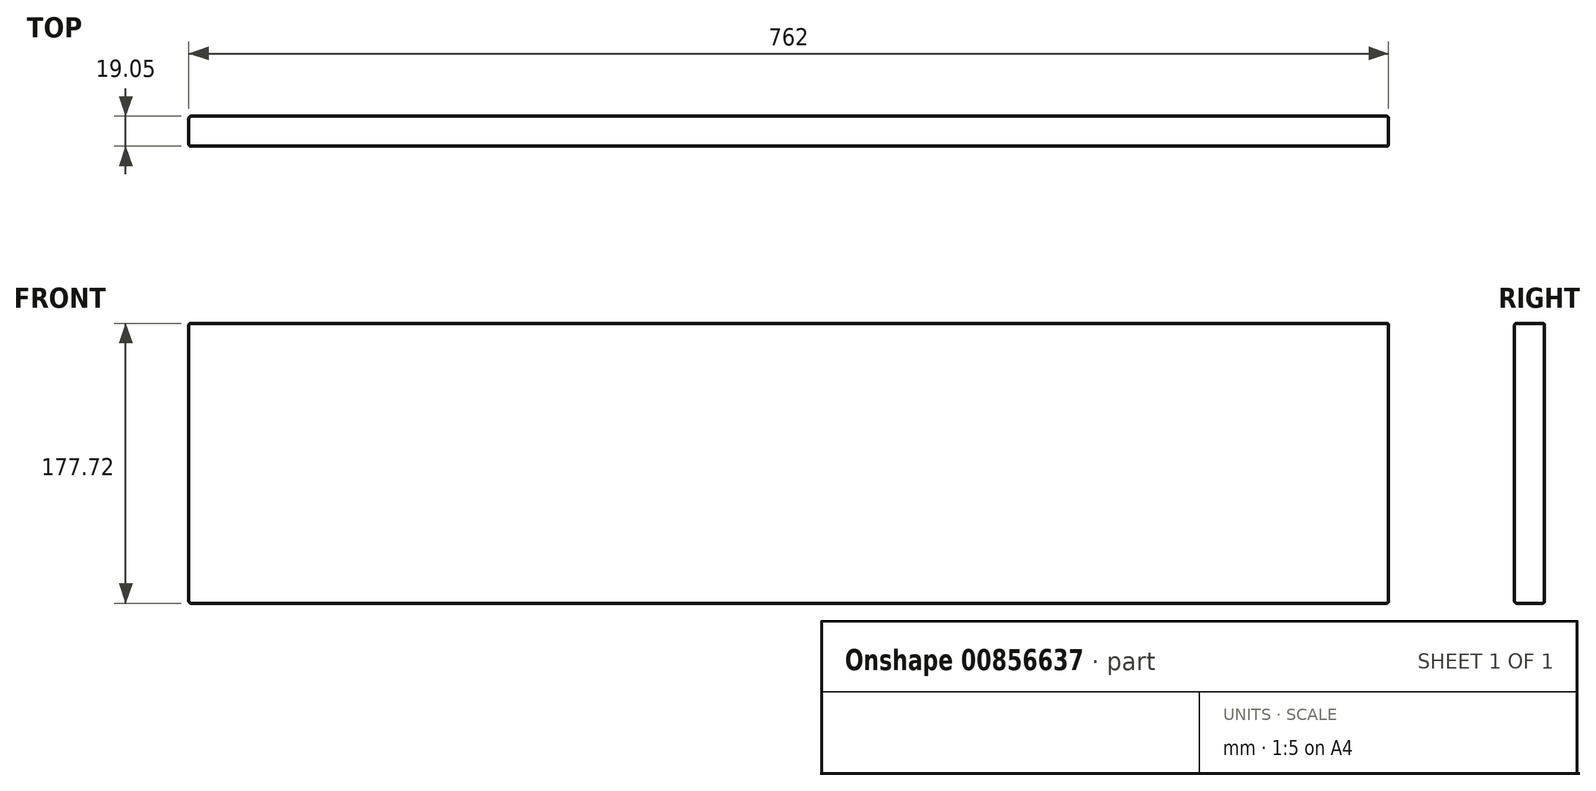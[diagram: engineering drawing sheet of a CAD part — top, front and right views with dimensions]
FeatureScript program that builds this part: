
annotation { "Feature Type Name" : "Feature", "Feature Type Description" : "" }
export const myFeature = defineFeature(function(context is Context, id is Id, definition is map)
    precondition{}
    {
        {
            var Q0;
            Q0=qCreatedBy(makeId("Front.planeOp"),FACE);
            var sketch = newSketch(context, id + "F0", { "sketchPlane" : qUnion([Q0])});
            skLineSegment(sketch, "E0.bottom", {"start": v(1208.67, 0) * mm, "end": v(2113.54, 0) * mm});
            skLineSegment(sketch, "E0.top", {"start": v(1208.67, 1778) * mm, "end": v(2113.54, 1778) * mm});
            skLineSegment(sketch, "E0.left", {"start": v(1208.67, 0) * mm, "end": v(1208.67, 1778) * mm});
            skLineSegment(sketch, "E0.right", {"start": v(2113.54, 0) * mm, "end": v(2113.54, 1778) * mm});
            skLineSegment(sketch, "E1.left", {"start": v(0, 0) * mm, "end": v(0.1, 863.6) * mm});
            skLineSegment(sketch, "E1.right", {"start": v(-1905, -2.15) * mm, "end": v(-1904.9, 861.45) * mm});
            skLineSegment(sketch, "E2.top", {"start": v(0.1, 901.7) * mm, "end": v(-2504.34, 901.7) * mm});
            skLineSegment(sketch, "E2.left", {"start": v(0.1, 863.6) * mm, "end": v(0.1, 901.7) * mm});
            skLineSegment(sketch, "E2.right", {"start": v(-2504.34, 863.6) * mm, "end": v(-2504.34, 901.7) * mm});
            skLineSegment(sketch, "E3", {"start": v(-1904.9, 1058.57) * mm, "end": v(-1904.9, -228.77) * mm, "construction": true});
            skLineSegment(sketch, "E4", {"start": v(0, 1058.57) * mm, "end": v(0, -228.77) * mm, "construction": true});
            skLineSegment(sketch, "E5.bottom", {"start": v(0, 0) * mm, "end": v(-381, 0) * mm});
            skLineSegment(sketch, "E5.left", {"start": v(0, 0) * mm, "end": v(0, 857.25) * mm});
            skLineSegment(sketch, "E6", {"start": v(-381, 0) * mm, "end": v(-387.35, 0) * mm, "construction": true});
            skLineSegment(sketch, "E7.bottom", {"start": v(-387.35, 0) * mm, "end": v(-1143, 0) * mm, "construction": true});
            skLineSegment(sketch, "E7.left", {"start": v(-387.35, 0) * mm, "end": v(-387.35, 736.6) * mm, "construction": true});
            skLineSegment(sketch, "E8", {"start": v(0, 0) * mm, "end": v(-1905, -2.15) * mm, "construction": true});
            skLineSegment(sketch, "E9.bottom", {"start": v(-387.35, 857.25) * mm, "end": v(-1143, 857.25) * mm, "construction": true});
            skLineSegment(sketch, "E9.top", {"start": v(-387.35, 121.5) * mm, "end": v(-1143, 120.65) * mm, "construction": true});
            skLineSegment(sketch, "E9.left", {"start": v(-387.35, 857.25) * mm, "end": v(-387.35, 121.5) * mm, "construction": true});
            skLineSegment(sketch, "E9.right", {"start": v(-1143, 857.25) * mm, "end": v(-1143, 120.65) * mm, "construction": true});
            skLineSegment(sketch, "E10", {"start": v(-1149.35, 857.25) * mm, "end": v(-1149.35, 120.65) * mm, "construction": true});
            skLineSegment(sketch, "E11.bottom", {"start": v(-1149.35, 857.25) * mm, "end": v(-1527.18, 857.25) * mm});
            skLineSegment(sketch, "E11.top", {"start": v(-1149.35, 82.55) * mm, "end": v(-1527.18, 82.55) * mm});
            skLineSegment(sketch, "E11.left", {"start": v(-1149.35, 857.25) * mm, "end": v(-1149.35, 82.55) * mm});
            skLineSegment(sketch, "E11.right", {"start": v(-1527.18, 857.25) * mm, "end": v(-1527.18, 82.55) * mm});
            skLineSegment(sketch, "E12", {"start": v(-1527.18, 82.55) * mm, "end": v(-1533.53, 82.54) * mm, "construction": true});
            skLineSegment(sketch, "E13.bottom", {"start": v(-1533.53, 82.54) * mm, "end": v(-1911.35, 82.54) * mm});
            skLineSegment(sketch, "E13.top", {"start": v(-1533.53, 857.25) * mm, "end": v(-1911.35, 857.25) * mm});
            skLineSegment(sketch, "E13.left", {"start": v(-1533.53, 82.54) * mm, "end": v(-1533.53, 857.25) * mm});
            skLineSegment(sketch, "E13.right", {"start": v(-1911.35, 82.54) * mm, "end": v(-1911.35, 857.25) * mm});
            skLineSegment(sketch, "E14", {"start": v(0, 857.25) * mm, "end": v(-2682.58, 857.25) * mm, "construction": true});
            skLineSegment(sketch, "E15.bottom", {"start": v(0, 857.25) * mm, "end": v(-381, 857.25) * mm});
            skLineSegment(sketch, "E15.top", {"start": v(0, 82.55) * mm, "end": v(-381, 82.55) * mm});
            skLineSegment(sketch, "E15.left", {"start": v(0, 857.25) * mm, "end": v(0, 82.55) * mm});
            skLineSegment(sketch, "E15.right", {"start": v(-381, 857.25) * mm, "end": v(-381, 82.55) * mm});
            skLineSegment(sketch, "E16.bottom", {"start": v(-387.35, 82.55) * mm, "end": v(-1143, 82.55) * mm});
            skLineSegment(sketch, "E16.top", {"start": v(-387.35, 115.22) * mm, "end": v(-1143, 115.22) * mm});
            skLineSegment(sketch, "E16.left", {"start": v(-387.35, 82.55) * mm, "end": v(-387.35, 115.22) * mm});
            skLineSegment(sketch, "E16.right", {"start": v(-1143, 82.55) * mm, "end": v(-1143, 115.22) * mm});
            skPoint(sketch, "E17", {"position": v(-765.18, 121.08) * mm});
            skPoint(sketch, "E18", {"position": v(-1530.35, 82.55) * mm});
            skPoint(sketch, "E18.positionSnap0", {"position": v(-1530.35, 82.55) * mm});
            skLineSegment(sketch, "E19", {"start": v(-765.18, 121.08) * mm, "end": v(-765.18, 1778) * mm, "construction": true});
            skLineSegment(sketch, "E20.bottom", {"start": v(-384.18, 2133.52) * mm, "end": v(-1146.18, 2133.52) * mm, "construction": true});
            skPoint(sketch, "E20.middle", {"position": v(-765.18, 1778) * mm});
            skLineSegment(sketch, "E21.bottom", {"start": v(-2504.34, 2438.4) * mm, "end": v(-1146.18, 2438.4) * mm});
            skLineSegment(sketch, "E21.top", {"start": v(-2504.34, 1778) * mm, "end": v(-1146.18, 1778) * mm});
            skLineSegment(sketch, "E21.left", {"start": v(-2504.34, 2438.4) * mm, "end": v(-2504.34, 1778) * mm});
            skLineSegment(sketch, "E21.right", {"start": v(-1146.18, 2438.4) * mm, "end": v(-1146.18, 1778) * mm});
            skLineSegment(sketch, "E22.bottom", {"start": v(0, 2438.4) * mm, "end": v(-384.18, 2438.4) * mm});
            skLineSegment(sketch, "E22.top", {"start": v(0, 1778) * mm, "end": v(-384.18, 1778) * mm});
            skLineSegment(sketch, "E22.left", {"start": v(0, 2438.4) * mm, "end": v(0, 1778) * mm});
            skLineSegment(sketch, "E22.right", {"start": v(-384.18, 2438.4) * mm, "end": v(-384.18, 1778) * mm});
            skLineSegment(sketch, "E23.bottom", {"start": v(-1146.18, 2133.52) * mm, "end": v(-384.18, 2133.52) * mm});
            skLineSegment(sketch, "E23.top", {"start": v(-1146.18, 1955.8) * mm, "end": v(-384.18, 1955.8) * mm});
            skLineSegment(sketch, "E23.left", {"start": v(-1146.18, 2133.52) * mm, "end": v(-1146.18, 1955.8) * mm});
            skLineSegment(sketch, "E23.right", {"start": v(-384.18, 2133.52) * mm, "end": v(-384.18, 1955.8) * mm});
            skLineSegment(sketch, "E24.bottom", {"start": v(-384.18, 1778) * mm, "end": v(0, 1778) * mm});
            skSolve(sketch);
        }
        {
            var Q0;
            {var subQ2=sQuery(id+"F0.wireOp",EDGE,"E23.bottom");Q0=makeQuery(id+"F0.imprint","IMPRINT",FACE,{"disambiguationData":[TD([[makeQuery(id+"F0.imprint","IMPRINT",EDGE,{"derivedFrom":subQ2}),-1.0]])]});}
            extrude(context, id + "F1", {"entities" : qUnion([Q0]), "depth" : 19.05 * mm, "offsetDistance" : 25.4 * mm});
        }
        {
            var Q0;
            Q0=makeQuery(id+"F1.opExtrude","CAP_FACE",FACE,{"disambiguationData":[OSD([sQuery(id+"F0.wireOp",EDGE,"E21.right"),sQuery(id+"F0.wireOp",EDGE,"E22.right"),sQuery(id+"F0.wireOp",EDGE,"E23.bottom"),sQuery(id+"F0.wireOp",EDGE,"E23.top")])],"isStart":false});
            var Q1;
            Q1=makeQuery(id+"F1.opExtrude","SWEPT_FACE",FACE,{"disambiguationData":[OSD([sQuery(id+"F0.wireOp",EDGE,"E23.bottom")])]});
            var Q2;
            Q2=makeQuery(id+"F1.opExtrude","SWEPT_FACE",FACE,{"disambiguationData":[OSD([sQuery(id+"F0.wireOp",EDGE,"E21.right")])]});
            var Q3;
            Q3=makeQuery(id+"F1.opExtrude","CAP_EDGE",EDGE,{"disambiguationData":[OSD([sQuery(id+"F0.wireOp",EDGE,"E22.right")])],"isStart":true});
            var Q4;
            Q4=makeQuery(id+"F1.opExtrude","CAP_EDGE",EDGE,{"disambiguationData":[OSD([sQuery(id+"F0.wireOp",EDGE,"E23.top")])],"isStart":true});
            var Q5;
            Q5=makeQuery(id+"F1.opExtrude","SWEPT_EDGE",EDGE,{"disambiguationData":[OSD([sQuery(id+"F0.wireOp",EDGE,"E22.right"),sQuery(id+"F0.wireOp",EDGE,"E23.top")])]});
            fillet(context, id + "F2", {"entities" : qUnion([Q0, Q1, Q2, Q3, Q4, Q5]), "radius" : 1.27 * mm, "tangentPropagation" : true, "allowEdgeOverflow" : false});
        }
    });
